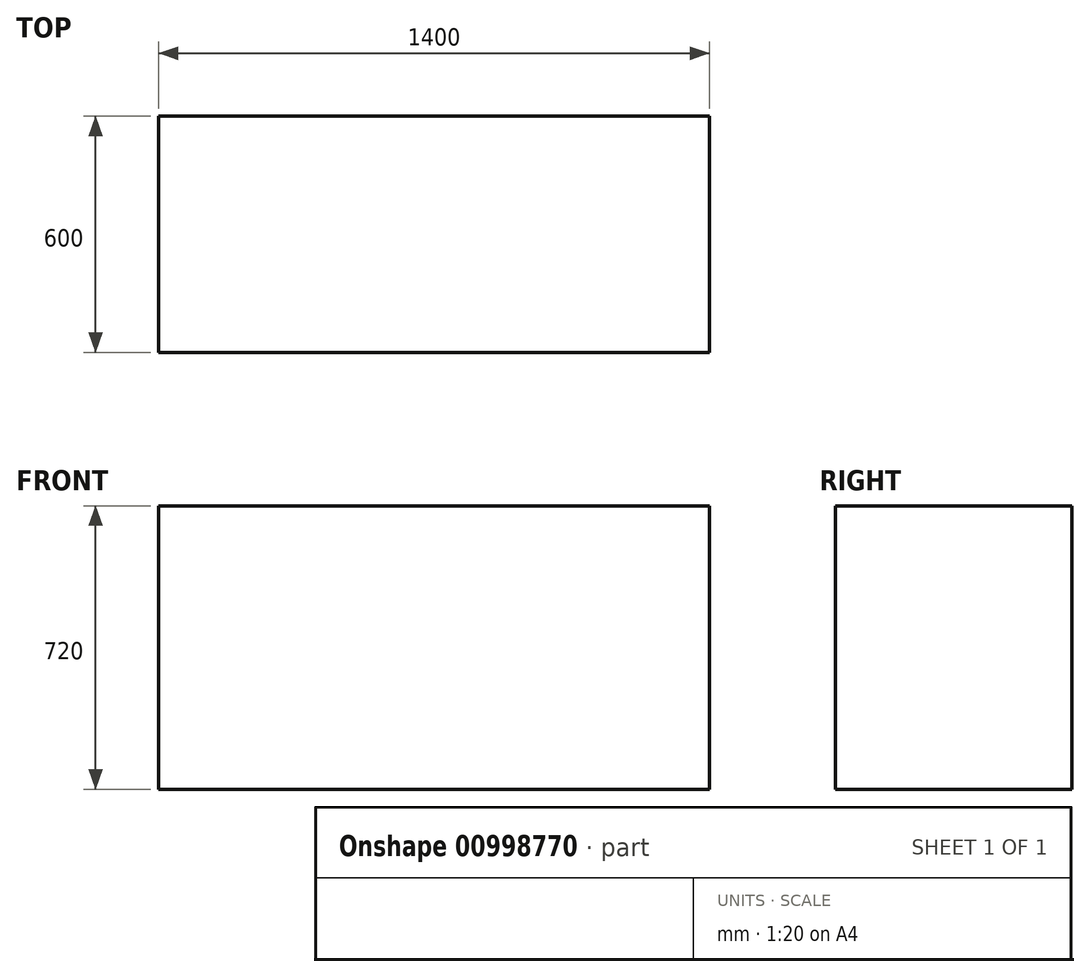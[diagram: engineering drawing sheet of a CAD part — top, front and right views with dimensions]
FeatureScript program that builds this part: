
annotation { "Feature Type Name" : "Feature", "Feature Type Description" : "" }
export const myFeature = defineFeature(function(context is Context, id is Id, definition is map)
    precondition{}
    {
        {
            var Q0;
            Q0=qCreatedBy(makeId("Top.planeOp"),FACE);
            var sketch = newSketch(context, id + "F0", { "sketchPlane" : qUnion([Q0])});
            skLineSegment(sketch, "E0.bottom", {"start": v(0, 0) * mm, "end": v(1400, 0) * mm});
            skLineSegment(sketch, "E0.top", {"start": v(0, 600) * mm, "end": v(1400, 600) * mm});
            skLineSegment(sketch, "E0.left", {"start": v(0, 0) * mm, "end": v(0, 600) * mm});
            skLineSegment(sketch, "E0.right", {"start": v(1400, 0) * mm, "end": v(1400, 600) * mm});
            skSolve(sketch);
        }
        {
            var Q0;
            Q0=makeQuery(id+"F0.imprint","IMPRINT",FACE,{"disambiguationData":[TD([[makeQuery(id+"F0.imprint","IMPRINT",EDGE,{"derivedFrom":sQuery(id+"F0.wireOp",EDGE,"E0.bottom")}),1.0]])]});
            extrude(context, id + "F1", {"entities" : qUnion([Q0]), "depth" : 720 * mm, "offsetDistance" : 25 * mm});
        }
    });
